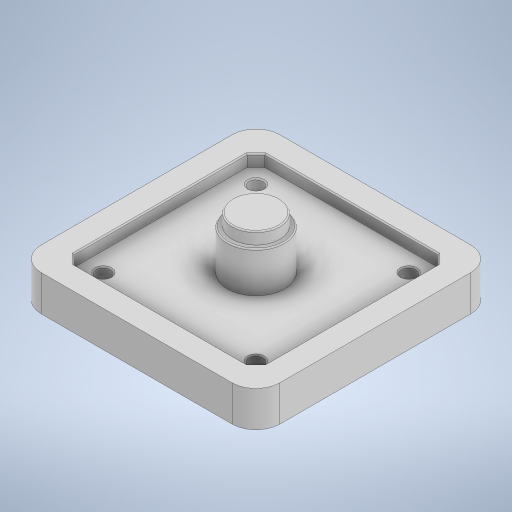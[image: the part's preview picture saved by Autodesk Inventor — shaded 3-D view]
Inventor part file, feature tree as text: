
AUTODESK INVENTOR PART (.ipt)
format: ipt  version: 2024.2 (Build 282272000, 272)  size: 323,584 bytes
history: native  units: mm
features: extrude x5, sketch x5, fillet x1, chamfer x1
ambient origin geometry x8: Origin, YZ Plane, XZ Plane, XY Plane, X Axis, Y Axis, Z Axis, Center Point
bodies: Solid1 (feature_tree)
feature tree (12):
  extrude  "Extrusion1"  Depth=100.0mm
  extrude  "Extrusion2"  Depth=10.0mm
  extrude  "Extrusion3"  Depth=15.0mm TaperAngle=0.0deg
  extrude  "Extrusion4"  Depth=80.0mm
  extrude  "Extrusion5"  Depth=0.5mm
  fillet  "Fillet1"  Radius=3.72656mm
  chamfer  "Chamfer1"  Distance=3.72656mm
  sketch  "Sketch1"  dims[d0=100.0mm d1=100.0mm]
  sketch  "Sketch2"  dims[d2=10.0mm d3=10.0mm]
  sketch  "Sketch3"  dims[d4=10.0mm d5=15.0mm d6=0.0mm]
  sketch  "Sketch4"  dims[d7=80.0mm d8=80.0mm]
  sketch  "Sketch5"  dims[d9=3.72656mm d10=3.72656mm d11=3.72656mm d12=3.72656mm d13=3.72656mm d14=3.72656mm d15=3.72656mm d16=3.72656mm d17=5.0mm d18=0.0mm d19=32.0mm d20=32.0mm d21=6.0mm d22=40.0mm d24=360.0deg d26=20.0mm d27=0.0mm d28=24.0mm d29=17.0mm d30=0.0mm d31=20.0mm d32=5.0mm d33=0.0mm d34=0.5mm d36=0.5mm d37=2.0mm d38=45.0deg]
